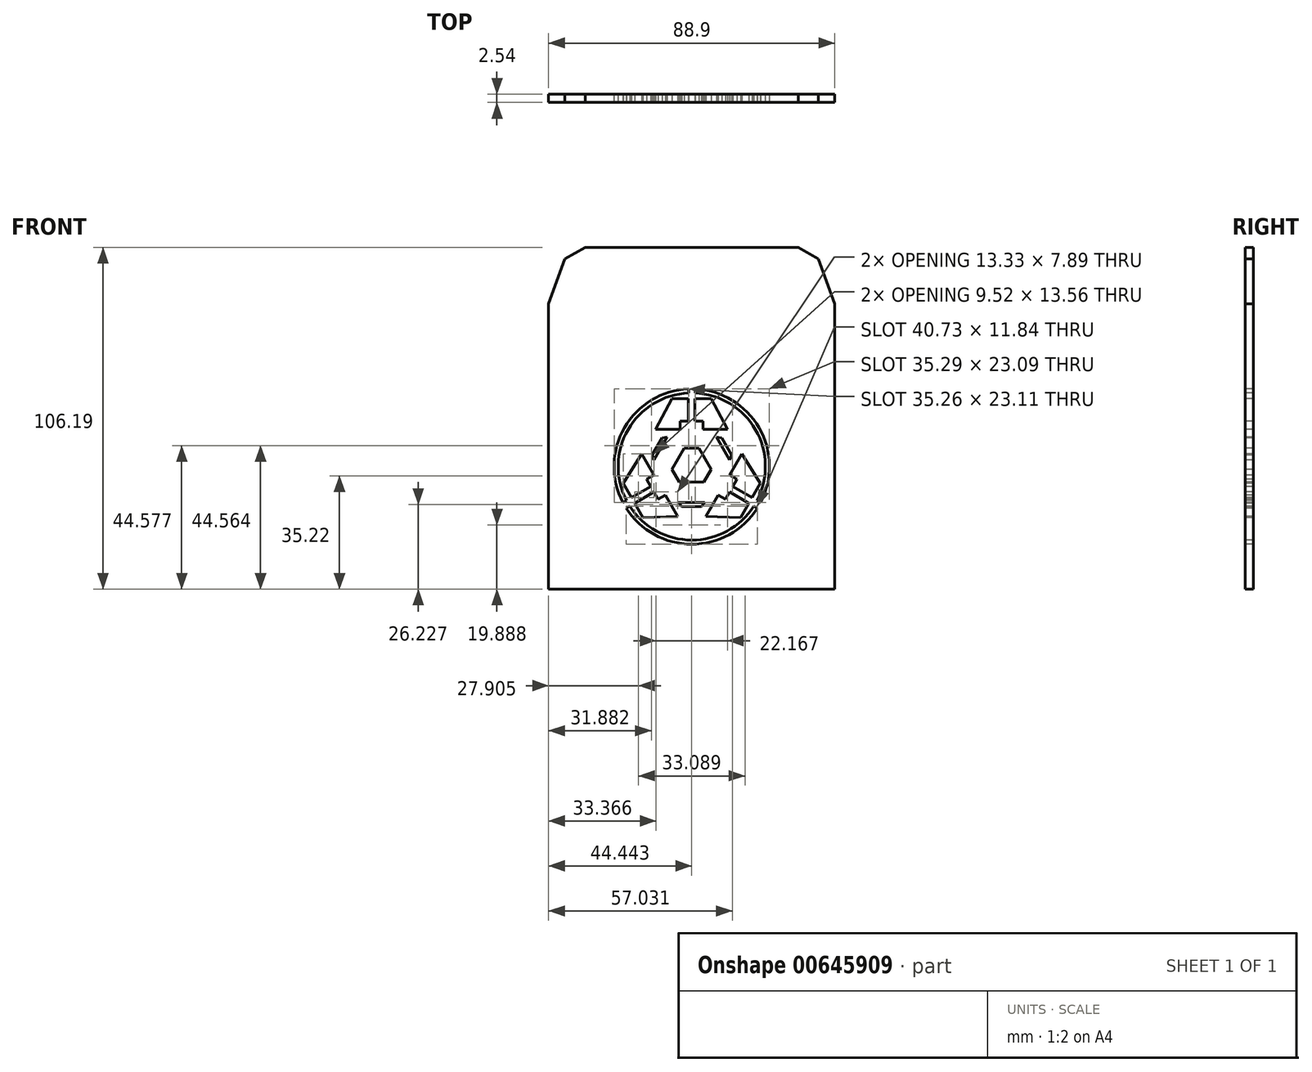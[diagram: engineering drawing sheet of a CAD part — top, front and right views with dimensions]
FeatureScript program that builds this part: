
annotation { "Feature Type Name" : "Feature", "Feature Type Description" : "" }
export const myFeature = defineFeature(function(context is Context, id is Id, definition is map)
    precondition{}
    {
        {
            var Q0;
            Q0=qCreatedBy(makeId("Front.planeOp"),FACE);
            var sketch = newSketch(context, id + "F0", { "sketchPlane" : qUnion([Q0])});
            skLineSegment(sketch, "E0", {"start": v(-88.9, 0) * mm, "end": v(-88.9, 88.61) * mm});
            skLineSegment(sketch, "E1", {"start": v(-88.9, 88.61) * mm, "end": v(-83.82, 102.57) * mm});
            skLineSegment(sketch, "E2", {"start": v(-83.82, 102.57) * mm, "end": v(-77.55, 106.19) * mm});
            skLineSegment(sketch, "E3", {"start": v(-77.55, 106.19) * mm, "end": v(-11.35, 106.19) * mm});
            skLineSegment(sketch, "E4", {"start": v(-11.35, 106.19) * mm, "end": v(-5.08, 102.57) * mm});
            skLineSegment(sketch, "E5", {"start": v(-5.08, 102.57) * mm, "end": v(0, 88.61) * mm});
            skLineSegment(sketch, "E6", {"start": v(0, 88.61) * mm, "end": v(0, 0) * mm});
            skLineSegment(sketch, "E7", {"start": v(0, 0) * mm, "end": v(-88.9, 0) * mm});
            skSolve(sketch);
        }
        {
            var Q0;
            Q0=makeQuery(id+"F0.imprint","IMPRINT",FACE,{"disambiguationData":[TD([[makeQuery(id+"F0.imprint","IMPRINT",EDGE,{"derivedFrom":sQuery(id+"F0.wireOp",EDGE,"E0")}),-1.0]])]});
            extrude(context, id + "F1", {"entities" : qUnion([Q0]), "oppositeDirection" : true, "depth" : 2.54 * mm, "offsetDistance" : 25.4 * mm});
        }
        {
            var Q0;
            Q0=makeQuery(id+"F1.opExtrude","CAP_FACE",FACE,{"disambiguationData":[OSD([sQuery(id+"F0.wireOp",EDGE,"E0"),sQuery(id+"F0.wireOp",EDGE,"E1"),sQuery(id+"F0.wireOp",EDGE,"E2"),sQuery(id+"F0.wireOp",EDGE,"E3"),sQuery(id+"F0.wireOp",EDGE,"E4"),sQuery(id+"F0.wireOp",EDGE,"E5"),sQuery(id+"F0.wireOp",EDGE,"E6"),sQuery(id+"F0.wireOp",EDGE,"E7")])],"isStart":true});
            var sketch = newSketch(context, id + "F2", { "sketchPlane" : qUnion([Q0])});
            skLineSegment(sketch, "E8", {"start": v(-45.47, 52.2) * mm, "end": v(-48, 52.2) * mm});
            skLineSegment(sketch, "E9", {"start": v(-48, 52.2) * mm, "end": v(-48, 49.66) * mm});
            skLineSegment(sketch, "E10", {"start": v(-48, 49.66) * mm, "end": v(-55.63, 49.66) * mm});
            skLineSegment(sketch, "E11", {"start": v(-43.43, 52.2) * mm, "end": v(-40.9, 52.2) * mm});
            skLineSegment(sketch, "E12", {"start": v(-40.9, 52.2) * mm, "end": v(-40.9, 49.66) * mm});
            skLineSegment(sketch, "E13", {"start": v(-40.9, 49.66) * mm, "end": v(-33.27, 49.66) * mm});
            skLineSegment(sketch, "E14", {"start": v(-55.63, 49.66) * mm, "end": v(-50.55, 59.18) * mm});
            skLineSegment(sketch, "E15", {"start": v(-33.27, 49.66) * mm, "end": v(-38.35, 59.18) * mm});
            skLineSegment(sketch, "E16", {"start": v(-50.55, 59.18) * mm, "end": v(-45.47, 59.18) * mm});
            skLineSegment(sketch, "E17", {"start": v(-45.47, 52.2) * mm, "end": v(-45.47, 59.18) * mm});
            skLineSegment(sketch, "E18", {"start": v(-43.43, 52.2) * mm, "end": v(-43.43, 59.18) * mm});
            skLineSegment(sketch, "E19.trimOffspring", {"start": v(-43.43, 59.18) * mm, "end": v(-38.35, 59.18) * mm});
            skLineSegment(sketch, "E20.1.0", {"start": v(-52.68, 29.24) * mm, "end": v(-48.87, 22.64) * mm});
            skLineSegment(sketch, "E20.1.1", {"start": v(-48.87, 22.64) * mm, "end": v(-59.66, 22.28) * mm});
            skLineSegment(sketch, "E20.1.2", {"start": v(-59.66, 22.28) * mm, "end": v(-62.2, 26.68) * mm});
            skLineSegment(sketch, "E20.1.3", {"start": v(-56.15, 30.17) * mm, "end": v(-62.2, 26.68) * mm});
            skLineSegment(sketch, "E20.1.4", {"start": v(-56.15, 30.17) * mm, "end": v(-54.88, 27.97) * mm});
            skLineSegment(sketch, "E20.1.5", {"start": v(-54.88, 27.97) * mm, "end": v(-52.68, 29.24) * mm});
            skLineSegment(sketch, "E20.1.6", {"start": v(-58.43, 34.13) * mm, "end": v(-56.24, 35.4) * mm});
            skLineSegment(sketch, "E20.1.7", {"start": v(-57.16, 31.93) * mm, "end": v(-58.43, 34.13) * mm});
            skLineSegment(sketch, "E20.1.8", {"start": v(-56.24, 35.4) * mm, "end": v(-60.05, 42) * mm});
            skLineSegment(sketch, "E20.1.9", {"start": v(-60.05, 42) * mm, "end": v(-65.75, 32.84) * mm});
            skLineSegment(sketch, "E20.1.10", {"start": v(-57.16, 31.93) * mm, "end": v(-63.21, 28.44) * mm});
            skLineSegment(sketch, "E20.1.11", {"start": v(-63.21, 28.44) * mm, "end": v(-65.75, 32.84) * mm});
            skLineSegment(sketch, "E20.2.0", {"start": v(-32.66, 35.4) * mm, "end": v(-28.85, 42) * mm});
            skLineSegment(sketch, "E20.2.1", {"start": v(-28.85, 42) * mm, "end": v(-23.15, 32.84) * mm});
            skLineSegment(sketch, "E20.2.2", {"start": v(-23.15, 32.84) * mm, "end": v(-25.69, 28.44) * mm});
            skLineSegment(sketch, "E20.2.3", {"start": v(-31.74, 31.93) * mm, "end": v(-25.69, 28.44) * mm});
            skLineSegment(sketch, "E20.2.4", {"start": v(-31.74, 31.93) * mm, "end": v(-30.47, 34.13) * mm});
            skLineSegment(sketch, "E20.2.5", {"start": v(-30.47, 34.13) * mm, "end": v(-32.66, 35.4) * mm});
            skLineSegment(sketch, "E20.2.6", {"start": v(-34.02, 27.97) * mm, "end": v(-36.22, 29.24) * mm});
            skLineSegment(sketch, "E20.2.7", {"start": v(-32.75, 30.17) * mm, "end": v(-34.02, 27.97) * mm});
            skLineSegment(sketch, "E20.2.8", {"start": v(-36.22, 29.24) * mm, "end": v(-40.03, 22.64) * mm});
            skLineSegment(sketch, "E20.2.9", {"start": v(-40.03, 22.64) * mm, "end": v(-29.24, 22.28) * mm});
            skLineSegment(sketch, "E20.2.10", {"start": v(-32.75, 30.17) * mm, "end": v(-26.7, 26.68) * mm});
            skLineSegment(sketch, "E20.2.11", {"start": v(-26.7, 26.68) * mm, "end": v(-29.24, 22.28) * mm});
            skPoint(sketch, "E20.center", {"position": v(-44.45, 38.1) * mm});
            skLineSegment(sketch, "E21", {"start": v(-50.55, 37.22) * mm, "end": v(-46.74, 43.82) * mm});
            skLineSegment(sketch, "E22", {"start": v(-46.74, 43.82) * mm, "end": v(-42.16, 43.82) * mm});
            skLineSegment(sketch, "E23", {"start": v(-42.16, 43.82) * mm, "end": v(-38.35, 37.22) * mm});
            skLineSegment(sketch, "E24", {"start": v(-38.35, 37.22) * mm, "end": v(-40.64, 33.26) * mm});
            skLineSegment(sketch, "E25", {"start": v(-40.64, 33.26) * mm, "end": v(-48.26, 33.26) * mm});
            skLineSegment(sketch, "E26", {"start": v(-48.26, 33.26) * mm, "end": v(-50.55, 37.22) * mm});
            skLineSegment(sketch, "E27", {"start": v(-52.07, 47.28) * mm, "end": v(-56.17, 40.18) * mm});
            skLineSegment(sketch, "E28", {"start": v(-56.17, 40.18) * mm, "end": v(-56.74, 41.73) * mm});
            skLineSegment(sketch, "E29", {"start": v(-56.74, 41.73) * mm, "end": v(-53.7, 47) * mm});
            skLineSegment(sketch, "E30", {"start": v(-53.7, 47) * mm, "end": v(-52.07, 47.28) * mm});
            skLineSegment(sketch, "E31.1.0", {"start": v(-47.53, 25.64) * mm, "end": v(-48.6, 26.91) * mm});
            skLineSegment(sketch, "E31.1.1", {"start": v(-41.45, 25.64) * mm, "end": v(-47.53, 25.64) * mm});
            skLineSegment(sketch, "E31.1.2", {"start": v(-48.6, 26.91) * mm, "end": v(-40.39, 26.91) * mm});
            skLineSegment(sketch, "E31.1.3", {"start": v(-40.39, 26.91) * mm, "end": v(-41.45, 25.64) * mm});
            skLineSegment(sketch, "E31.2.0", {"start": v(-32.12, 41.67) * mm, "end": v(-32.69, 40.1) * mm});
            skLineSegment(sketch, "E31.2.1", {"start": v(-35.16, 46.93) * mm, "end": v(-32.12, 41.67) * mm});
            skLineSegment(sketch, "E31.2.2", {"start": v(-32.69, 40.1) * mm, "end": v(-36.8, 47.21) * mm});
            skLineSegment(sketch, "E31.2.3", {"start": v(-36.8, 47.21) * mm, "end": v(-35.16, 46.93) * mm});
            skArc(sketch, "E32", {"start": v(-45.46, 62.2) * mm, "mid": v(-65.34, 50.18) * mm, "end": v(-65.85, 26.94) * mm});
            skLineSegment(sketch, "E33", {"start": v(-45.46, 60.94) * mm, "end": v(-45.46, 62.2) * mm});
            skLineSegment(sketch, "E34", {"start": v(-43.41, 60.94) * mm, "end": v(-43.41, 62.2) * mm});
            skLineSegment(sketch, "E35.1.0", {"start": v(-63.72, 25.8) * mm, "end": v(-64.82, 25.17) * mm});
            skLineSegment(sketch, "E35.1.1", {"start": v(-64.75, 27.58) * mm, "end": v(-65.85, 26.94) * mm});
            skLineSegment(sketch, "E35.2.0", {"start": v(-24.17, 27.56) * mm, "end": v(-23.07, 26.92) * mm});
            skLineSegment(sketch, "E35.2.1", {"start": v(-25.2, 25.78) * mm, "end": v(-24.1, 25.15) * mm});
            skArc(sketch, "E36.trimOffspring", {"start": v(-64.82, 25.17) * mm, "mid": v(-44.46, 13.97) * mm, "end": v(-24.1, 25.15) * mm});
            skArc(sketch, "E37.trimOffspring", {"start": v(-23.07, 26.92) * mm, "mid": v(-23.55, 50.15) * mm, "end": v(-43.41, 62.2) * mm});
            skArc(sketch, "E38", {"start": v(-24.17, 27.56) * mm, "mid": v(-24.65, 49.52) * mm, "end": v(-43.41, 60.94) * mm});
            skArc(sketch, "E39.trimOffspring", {"start": v(-63.72, 25.8) * mm, "mid": v(-44.46, 15.24) * mm, "end": v(-25.2, 25.78) * mm});
            skArc(sketch, "E40.trimOffspring", {"start": v(-45.46, 60.94) * mm, "mid": v(-64.24, 49.54) * mm, "end": v(-64.75, 27.58) * mm});
            skSolve(sketch);
        }
        {
            var Q0;
            {var subQ0=sQuery(id+"F2.wireOp",EDGE,"E32");Q0=makeQuery(id+"F2.imprint","IMPRINT",FACE,{"disambiguationData":[TD([[makeQuery(id+"F2.imprint","IMPRINT",EDGE,{"derivedFrom":subQ0}),1.0]])]});}
            var Q1;
            Q1=makeQuery(id+"F2.imprint","IMPRINT",FACE,{"disambiguationData":[TD([[makeQuery(id+"F2.imprint","IMPRINT",EDGE,{"derivedFrom":sQuery(id+"F2.wireOp",EDGE,"E20.1.6")}),1.0]])]});
            var Q2;
            Q2=makeQuery(id+"F2.imprint","IMPRINT",FACE,{"disambiguationData":[TD([[makeQuery(id+"F2.imprint","IMPRINT",EDGE,{"derivedFrom":sQuery(id+"F2.wireOp",EDGE,"E21")}),-1.0]])]});
            var Q3;
            Q3=makeQuery(id+"F2.imprint","IMPRINT",FACE,{"disambiguationData":[TD([[makeQuery(id+"F2.imprint","IMPRINT",EDGE,{"derivedFrom":sQuery(id+"F2.wireOp",EDGE,"E8")}),-1.0]])]});
            var Q4;
            Q4=makeQuery(id+"F2.imprint","IMPRINT",FACE,{"disambiguationData":[TD([[makeQuery(id+"F2.imprint","IMPRINT",EDGE,{"derivedFrom":sQuery(id+"F2.wireOp",EDGE,"E11")}),1.0]])]});
            var Q5;
            Q5=makeQuery(id+"F2.imprint","IMPRINT",FACE,{"disambiguationData":[TD([[makeQuery(id+"F2.imprint","IMPRINT",EDGE,{"derivedFrom":sQuery(id+"F2.wireOp",EDGE,"E20.2.0")}),-1.0]])]});
            var Q6;
            Q6=makeQuery(id+"F2.imprint","IMPRINT",FACE,{"disambiguationData":[TD([[makeQuery(id+"F2.imprint","IMPRINT",EDGE,{"derivedFrom":sQuery(id+"F2.wireOp",EDGE,"E20.2.6")}),1.0]])]});
            var Q7;
            Q7=makeQuery(id+"F2.imprint","IMPRINT",FACE,{"disambiguationData":[TD([[makeQuery(id+"F2.imprint","IMPRINT",EDGE,{"derivedFrom":sQuery(id+"F2.wireOp",EDGE,"E20.1.0")}),-1.0]])]});
            var Q8;
            Q8=makeQuery(id+"F2.imprint","IMPRINT",FACE,{"disambiguationData":[TD([[makeQuery(id+"F2.imprint","IMPRINT",EDGE,{"derivedFrom":sQuery(id+"F2.wireOp",EDGE,"E35.1.0")}),1.0]])]});
            var Q9;
            Q9=makeQuery(id+"F2.imprint","IMPRINT",FACE,{"disambiguationData":[TD([[makeQuery(id+"F2.imprint","IMPRINT",EDGE,{"derivedFrom":sQuery(id+"F2.wireOp",EDGE,"E31.2.0")}),-1.0]])]});
            var Q10;
            Q10=makeQuery(id+"F2.imprint","IMPRINT",FACE,{"disambiguationData":[TD([[makeQuery(id+"F2.imprint","IMPRINT",EDGE,{"derivedFrom":sQuery(id+"F2.wireOp",EDGE,"E27")}),-1.0]])]});
            var Q11;
            Q11=makeQuery(id+"F2.imprint","IMPRINT",FACE,{"disambiguationData":[TD([[makeQuery(id+"F2.imprint","IMPRINT",EDGE,{"derivedFrom":sQuery(id+"F2.wireOp",EDGE,"E31.1.0")}),-1.0]])]});
            var Q12;
            Q12=makeQuery(id+"F2.imprint","IMPRINT",FACE,{"disambiguationData":[TD([[makeQuery(id+"F2.imprint","IMPRINT",EDGE,{"derivedFrom":sQuery(id+"F2.wireOp",EDGE,"E35.2.0")}),1.0]])]});
            extrude(context, id + "F3", {"entities" : qUnion([Q0, Q1, Q2, Q3, Q4, Q5, Q6, Q7, Q8, Q9, Q10, Q11, Q12]), "operationType" : NewBodyOperationType.REMOVE, "oppositeDirection" : true, "depth" : 25.4 * mm, "offsetDistance" : 25.4 * mm});
        }
    });
